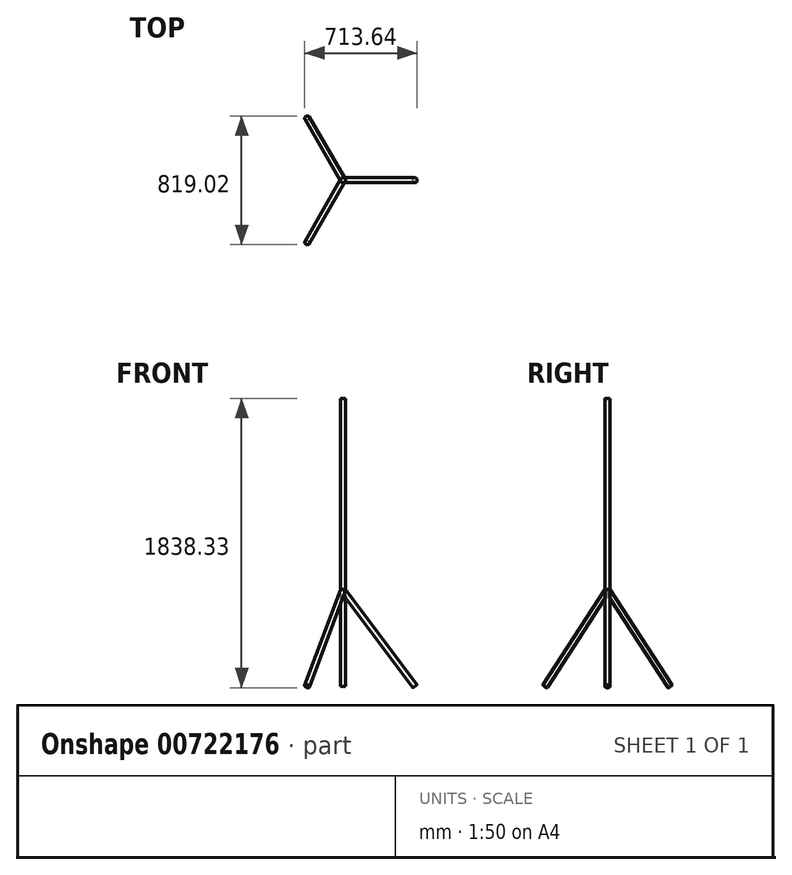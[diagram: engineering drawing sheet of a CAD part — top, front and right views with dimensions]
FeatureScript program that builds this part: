
annotation { "Feature Type Name" : "Feature", "Feature Type Description" : "" }
export const myFeature = defineFeature(function(context is Context, id is Id, definition is map)
    precondition{}
    {
        {
            var Q0;
            Q0=qCreatedBy(makeId("Top.planeOp"),FACE);
            var sketch = newSketch(context, id + "F0", { "sketchPlane" : qUnion([Q0])});
            skCircle(sketch, "E0", {"center": v(0, 0) * mm, "radius": 15.88 * mm});
            skSolve(sketch);
        }
        {
            var Q0;
            Q0 = qSketchRegion(id + "F0", true);
            extrude(context, id + "F1", {"entities" : qUnion([Q0]), "depth" : 1828.8 * mm, "offsetDistance" : 25.4 * mm});
        }
        {
            var Q0;
            Q0=qCreatedBy(makeId("Front.planeOp"),FACE);
            var sketch = newSketch(context, id + "F2", { "sketchPlane" : qUnion([Q0])});
            skLineSegment(sketch, "E1", {"start": v(0, 0) * mm, "end": v(0, 609.6) * mm, "construction": true});
            skLineSegment(sketch, "E2", {"start": v(0, 609.6) * mm, "end": v(457.2, 0) * mm});
            skLineSegment(sketch, "E3", {"start": v(457.2, 0) * mm, "end": v(0, 0) * mm, "construction": true});
            skSolve(sketch);
        }
        {
            var Q0;
            Q0=sQuery(id+"F2.wireOp",VERTEX,"E2.end");
            var Q1;
            Q1=sQuery(id+"F2.wireOp",EDGE,"E2");
            cPlane(context, id + "F3", {"entities" : qUnion([Q0, Q1]), "cplaneType" : CPlaneType.CURVE_POINT, "offset" : 25.4 * mm, "width" : 152.4 * mm, "height" : 152.4 * mm});
        }
        {
            var Q0;
            Q0=qCreatedBy(id+"F3.planeOp",FACE);
            var sketch = newSketch(context, id + "F4", { "sketchPlane" : qUnion([Q0])});
            skCircle(sketch, "E4", {"center": v(365.76, 0) * mm, "radius": 15.88 * mm});
            skSolve(sketch);
        }
        {
            var Q0;
            Q0=makeQuery(id+"F4.imprint","IMPRINT",FACE,{"disambiguationData":[TD([[makeQuery(id+"F4.imprint","IMPRINT",EDGE,{"derivedFrom":sQuery(id+"F4.wireOp",EDGE,"E4")}),1.0]])]});
            var Q1;
            Q1=sQuery(id+"F2.wireOp",EDGE,"E2");
            sweep(context, id + "F5", {"operationType" : NewBodyOperationType.ADD, "profiles" : qUnion([Q0]), "path" : qUnion([Q1])});
        }
        {
            var Q0;
            Q0=makeQuery(id+"F1.opExtrude","SWEPT_BODY",BODY,{"disambiguationData":[OSD([sQuery(id+"F0.wireOp",EDGE,"E0")])]});
            var Q1;
            Q1=makeQuery(id+"F1.opExtrude","SWEPT_FACE",FACE,{"disambiguationData":[OSD([sQuery(id+"F0.wireOp",EDGE,"E0")])]});
            circularPattern(context, id + "F6", {"operationType" : NewBodyOperationType.ADD, "entities" : qUnion([Q0]), "axis" : qUnion([Q1]), "angle" : 360 * degree, "instanceCount" : 3, "equalSpace" : true});
        }
    });
